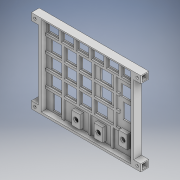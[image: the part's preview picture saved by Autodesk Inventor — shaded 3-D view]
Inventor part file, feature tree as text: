
AUTODESK INVENTOR PART (.ipt)
format: ipt  version: 2022 (Build 260153000, 153)  size: 935,424 bytes
history: native  units: in
note: dims shown in document units (in); Inventor stores cm internally (conversion verified against a paired STEP export)
features: extrude x32, sketch x26, projected_geometry x19
ambient origin geometry x8: Origin, YZ Plane, XZ Plane, XY Plane, X Axis, Y Axis, Z Axis, Center Point
bodies: Solid1 (feature_tree)
feature tree (77):
  extrude  "Extrusion1"  Depth=0.555in
  extrude  "Extrusion2"  Depth=0.555in
  extrude  "Extrusion3"  Depth=0.555in
  extrude  "Extrusion4"  Depth=0.555in
  extrude  "Extrusion5"  Depth=0.555in
  extrude  "Extrusion6"  Depth=0.555in
  extrude  "Extrusion7"  Depth=0.555in
  extrude  "Extrusion8"  Depth=0.555in
  extrude  "Extrusion9"  Depth=0.555in
  sketch  "Sketch10"  dims[d77=0.555in d78=0.5554in]
  extrude  "Extrusion10"  Depth=0.5554in
  extrude  "Extrusion11"  Depth=0.555in
  extrude  "Extrusion12"  Depth=0.555in
  sketch  "Sketch12"  dims[d81=0.555in d82=0.555in]
  sketch  "Sketch13"  dims[d83=0.555in d84=0.555in]
  extrude  "Extrusion13"  Depth=0.555in
  extrude  "Extrusion14"  Depth=0.555in
  extrude  "Extrusion15"  Depth=0.555in
  extrude  "Extrusion16"  Depth=0.555in
  extrude  "Extrusion17"  Depth=0.7614in
  extrude  "Extrusion18"  Depth=0.065in
  extrude  "Extrusion19"  Depth=0.1181in
  sketch  "Sketch18"  dims[d93=0.065in d94=0.0in d102=0.0591in]
  extrude  "Extrusion20"  Depth=0.0787in TaperAngle=0.0deg
  extrude  "Extrusion21"  Depth=4.4802in
  extrude  "Extrusion22"  Depth=0.04in TaperAngle=0.0deg
  extrude  "Extrusion23"  Depth=0.415in TaperAngle=0.0deg
  extrude  "Extrusion24"  Depth=0.0787in TaperAngle=0.0deg
  extrude  "Extrusion26"  Depth=0.0512in
  extrude  "Extrusion27"  Depth=0.0512in
  extrude  "Extrusion28"  Depth=0.252in
  sketch  "Sketch26"  dims[d132=4.4594in d133=0.0in d134=0.0512in]
  sketch  "Sketch27"  dims[d135=0.252in d136=0.0512in d137=0.252in d138=0.3543in d139=0.0in d140=6.1457in d141=0.0in d142=0.3543in d143=0.0in d144=0.2402in d145=0.2402in d146=0.2953in d147=0.5354in d148=0.2953in d149=0.063in d150=0.063in d151=0.3937in d152=0.0in d153=0.3799in d154=0.0in d155=0.3799in d156=0.0in d157=0.315in d158=0.0in d159=0.315in d160=0.0in d161=0.1969in d162=0.0in d163=0.0925in d164=0.0in d165=0.2402in d166=0.065in d167=0.0in d168=0.065in d169=0.0in d170=0.0748in d171=0.0in d172=0.6998in d173=0.0in d174=0.2067in d175=0.3543in d176=0.0in d180=0.0547in d181=0.0in d182=0.0669in d183=0.3543in d184=0.0in d185=0.3543in d186=0.0in d187=0.065in d188=0.0in d189=0.065in d190=0.0in d191=0.3937in d192=0.0in d193=0.3937in d194=0.0in d195=0.3937in d196=0.0in]
  extrude  "Extrusion29"  Depth=0.3543in TaperAngle=0.0deg
  extrude  "Extrusion30"  Depth=0.3937in TaperAngle=0.0deg
  extrude  "Extrusion31"  Depth=0.3543in TaperAngle=0.0deg
  extrude  "Extrusion32"  Depth=0.3937in
  extrude  "Extrusion33"  Depth=0.3937in
  sketch  "Sketch1"  dims[d56=0.555in d57=0.555in]
  sketch  "Sketch2"  dims[d58=0.555in d59=0.555in]
  projected_geometry  "Projected Loop1"
  sketch  "Sketch3"  dims[d60=0.555in d61=0.555in]
  sketch  "Sketch4"  dims[d62=0.555in d63=0.555in]
  sketch  "Sketch5"  dims[d65=0.555in d66=0.555in]
  sketch  "Sketch6"  dims[d67=0.555in d68=0.555in]
  sketch  "Sketch7"  dims[d69=0.555in d72=0.555in]
  sketch  "Sketch8"  dims[d73=0.555in d74=0.555in]
  projected_geometry  "Projected Loop2"
  projected_geometry  "Projected Loop3"
  projected_geometry  "Projected Loop4"
  projected_geometry  "Projected Loop5"
  sketch  "Sketch9"  dims[d75=0.555in d76=0.555in]
  sketch  "Sketch11"  dims[d79=0.555in d80=0.555in]
  projected_geometry  "Projected Loop6"
  projected_geometry  "Projected Loop7"
  projected_geometry  "Projected Loop8"
  sketch  "Sketch14"  dims[d85=0.555in d86=0.555in]
  projected_geometry  "Projected Loop9"
  projected_geometry  "Projected Loop10"
  sketch  "Sketch15"  dims[d87=0.555in d88=0.555in]
  sketch  "Sketch16"  dims[d89=0.5554in d90=0.555in]
  sketch  "Sketch17"  dims[d91=0.5543in d92=0.7614in]
  sketch  "Sketch19"  dims[d103=0.0591in d114=0.1181in]
  projected_geometry  "Projected Loop11"
  projected_geometry  "Projected Loop12"
  projected_geometry  "Projected Loop13"
  projected_geometry  "Projected Loop14"
  sketch  "Sketch20"  dims[d115=0.1181in d116=0.0787in d117=0.0in]
  sketch  "Sketch21"  dims[d118=0.0787in d119=0.0in d120=4.4802in]
  projected_geometry  "Projected Loop15"
  projected_geometry  "Projected Loop16"
  sketch  "Sketch23"  dims[d121=0.4724in d122=0.0in d123=0.04in d124=0.0in]
  sketch  "Sketch24"  dims[d125=0.1299in d126=0.415in d127=0.0in]
  sketch  "Sketch25"  dims[d128=0.0787in d129=0.0in d130=0.1031in d131=0.0in]
  projected_geometry  "Projected Loop19"
  projected_geometry  "Projected Loop20"
  projected_geometry  "Projected Loop21"
